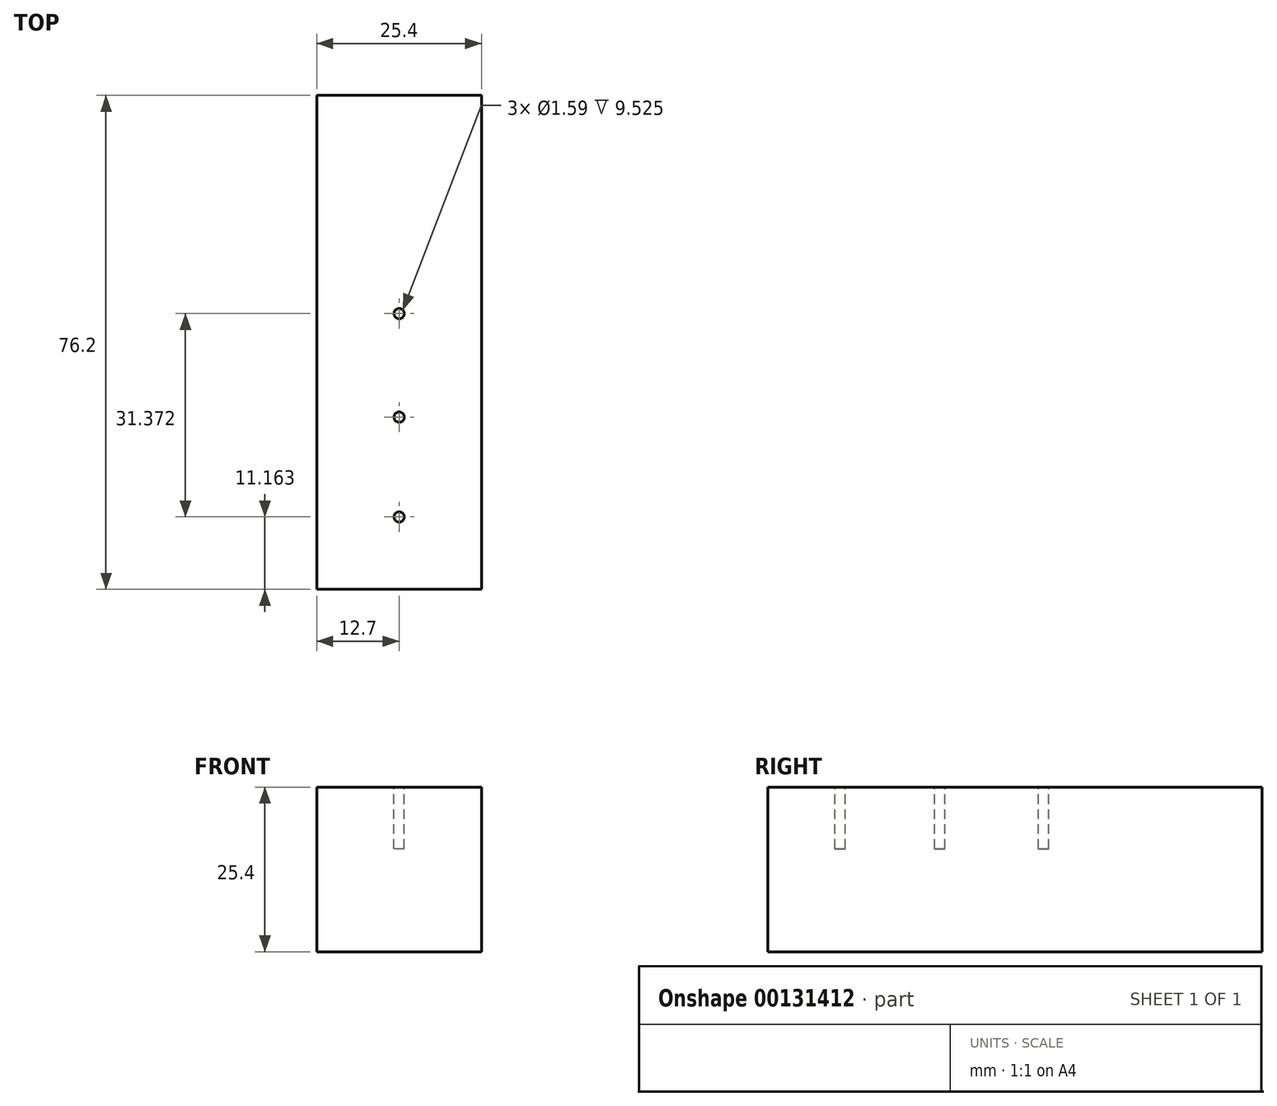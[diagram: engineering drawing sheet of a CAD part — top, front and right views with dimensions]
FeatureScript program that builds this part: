
annotation { "Feature Type Name" : "Feature", "Feature Type Description" : "" }
export const myFeature = defineFeature(function(context is Context, id is Id, definition is map)
    precondition{}
    {
        {
            var Q0;
            Q0=qCreatedBy(makeId("Front.planeOp"),FACE);
            var sketch = newSketch(context, id + "F0", { "sketchPlane" : qUnion([Q0])});
            skLineSegment(sketch, "E0.bottom", {"start": v(-12.7, 12.7) * mm, "end": v(12.7, 12.7) * mm});
            skLineSegment(sketch, "E0.top", {"start": v(-12.7, -12.7) * mm, "end": v(12.7, -12.7) * mm});
            skLineSegment(sketch, "E0.left", {"start": v(-12.7, 12.7) * mm, "end": v(-12.7, -12.7) * mm});
            skLineSegment(sketch, "E0.right", {"start": v(12.7, 12.7) * mm, "end": v(12.7, -12.7) * mm});
            skSolve(sketch);
        }
        {
            var Q0;
            Q0 = qSketchRegion(id + "F0", true);
            extrude(context, id + "F1", {"entities" : qUnion([Q0]), "depth" : 76.2 * mm});
        }
        {
            var Q0;
            Q0=makeQuery(id+"F1.opExtrude","SWEPT_FACE",FACE,{"disambiguationData":[OSD([sQuery(id+"F0.wireOp",EDGE,"E0.bottom")])]});
            var sketch = newSketch(context, id + "F2", { "sketchPlane" : qUnion([Q0])});
            skLineSegment(sketch, "E1", {"start": v(0, 0) * mm, "end": v(0, -76.2) * mm, "construction": true});
            skCircle(sketch, "E2", {"center": v(0, -33.66) * mm, "radius": 0.8 * mm});
            skCircle(sketch, "E3", {"center": v(0, -49.63) * mm, "radius": 0.8 * mm});
            skCircle(sketch, "E4", {"center": v(0, -65.04) * mm, "radius": 0.8 * mm});
            skSolve(sketch);
        }
        {
            var Q0;
            Q0 = qSketchRegion(id + "F2", true);
            extrude(context, id + "F3", {"entities" : qUnion([Q0]), "operationType" : NewBodyOperationType.REMOVE, "oppositeDirection" : true, "depth" : 9.52 * mm});
        }
    });
